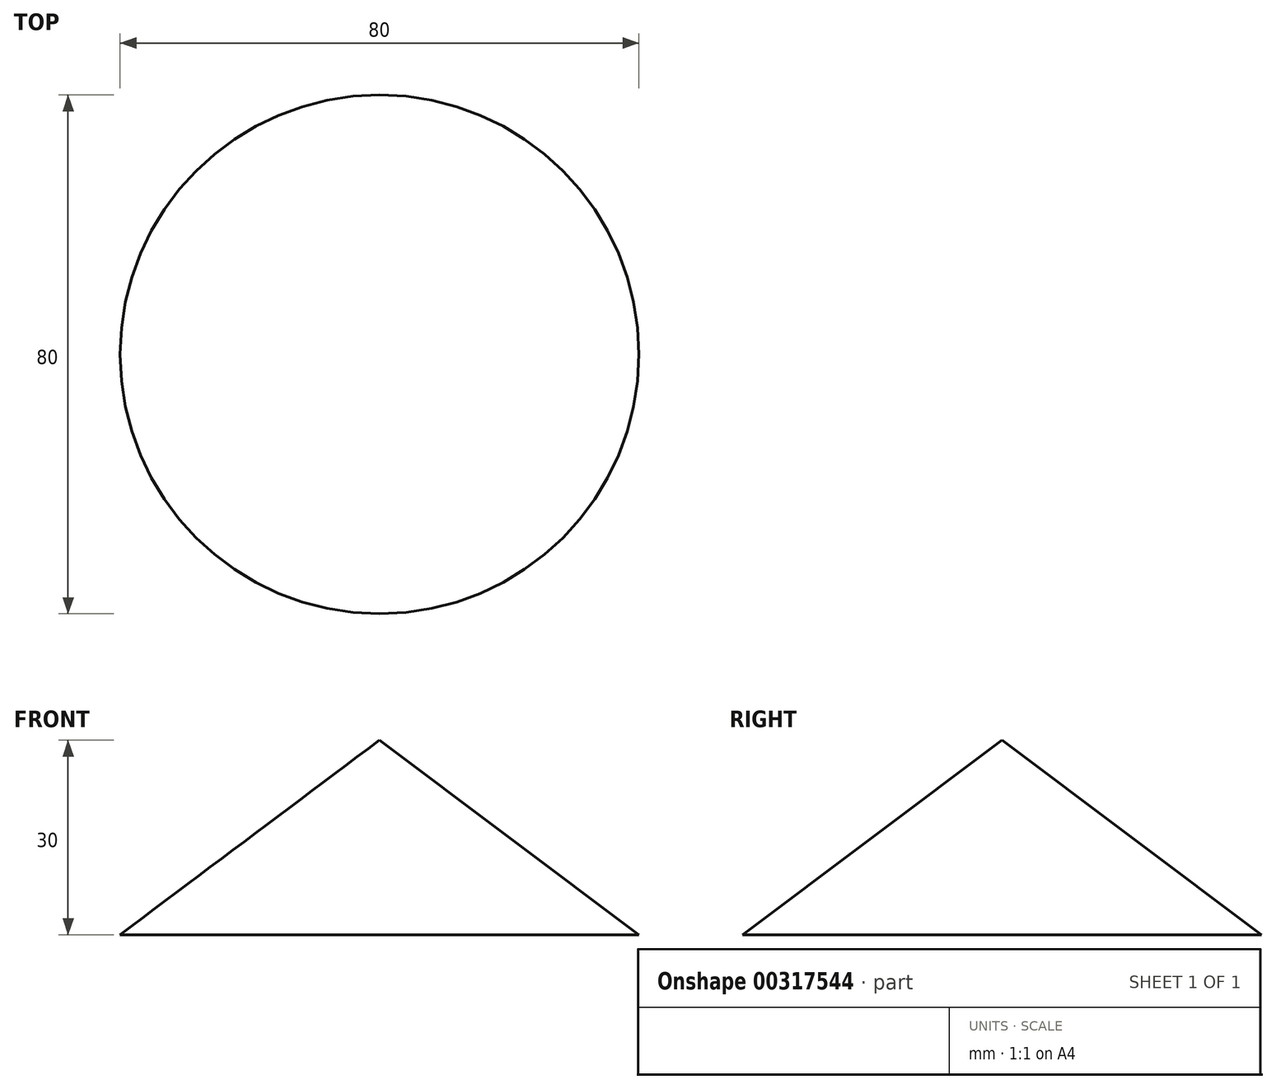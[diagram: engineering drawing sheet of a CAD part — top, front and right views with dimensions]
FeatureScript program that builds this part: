
annotation { "Feature Type Name" : "Feature", "Feature Type Description" : "" }
export const myFeature = defineFeature(function(context is Context, id is Id, definition is map)
    precondition{}
    {
        {
            var Q0;
            Q0=qCreatedBy(makeId("Front.planeOp"),FACE);
            var sketch = newSketch(context, id + "F0", { "sketchPlane" : qUnion([Q0])});
            skLineSegment(sketch, "E0", {"start": v(0, 0) * mm, "end": v(0, 30) * mm});
            skLineSegment(sketch, "E1", {"start": v(0, 30) * mm, "end": v(40, 0) * mm});
            skLineSegment(sketch, "E2", {"start": v(40, 0) * mm, "end": v(0, 0) * mm});
            skLineSegment(sketch, "E3", {"start": v(0, 48.62) * mm, "end": v(0, -29.6) * mm, "construction": true});
            skSolve(sketch);
        }
        {
            var Q0;
            Q0 = qSketchRegion(id + "F0", true);
            var Q1;
            Q1=sQuery(id+"F0.wireOp",EDGE,"E3");
            revolve(context, id + "F1", {"entities" : qUnion([Q0]), "axis" : qUnion([Q1]), "revolveType" : RevolveType.FULL});
        }
    });
